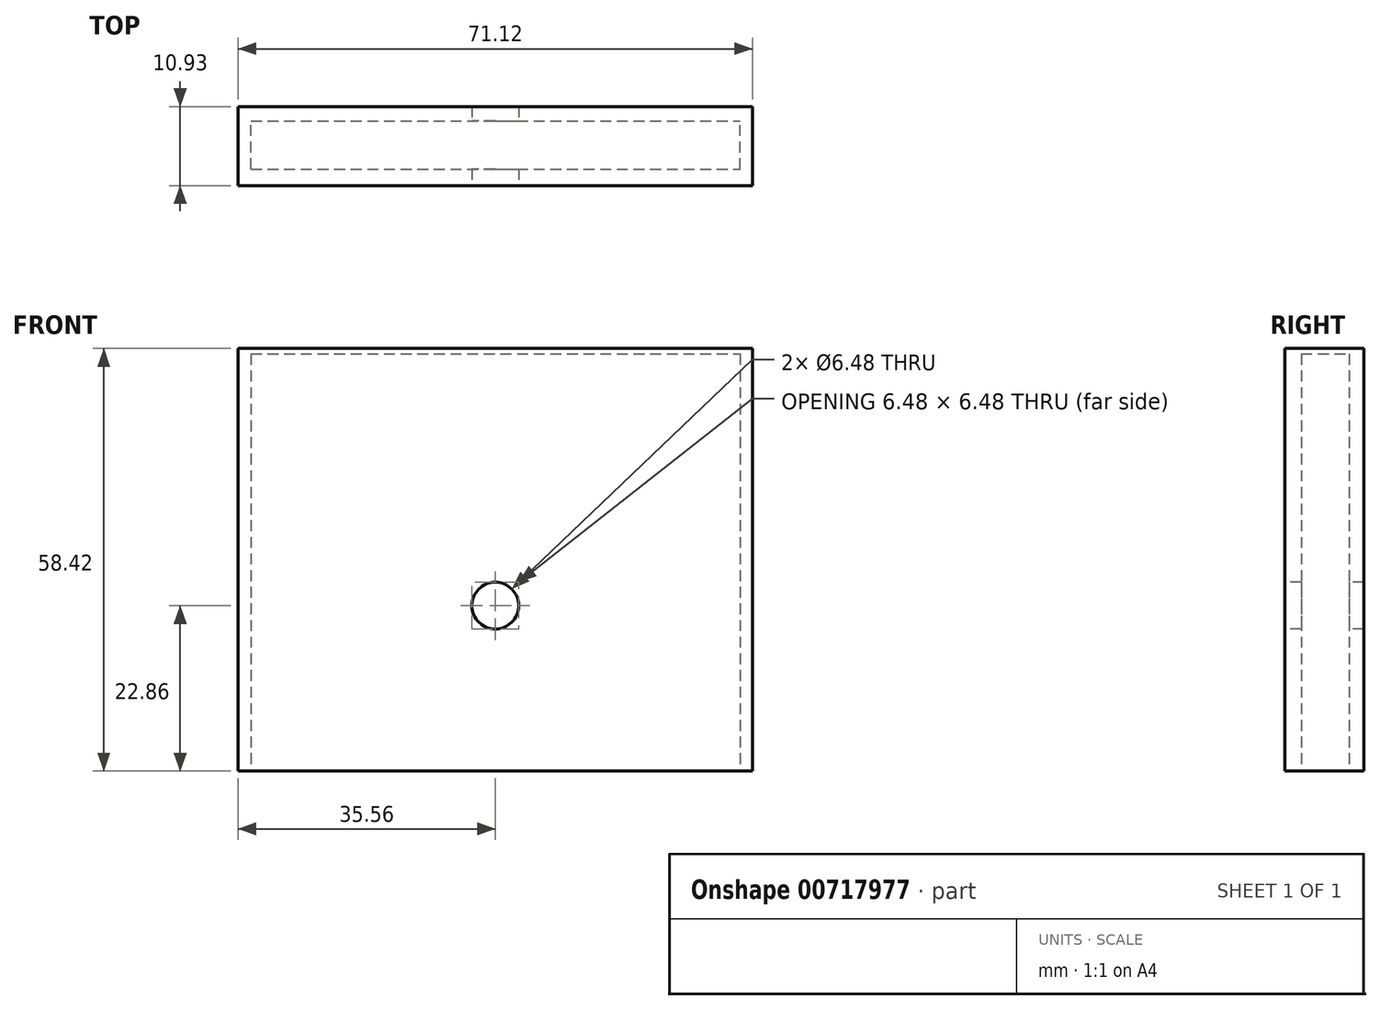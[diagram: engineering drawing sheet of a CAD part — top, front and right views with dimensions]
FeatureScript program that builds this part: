
annotation { "Feature Type Name" : "Feature", "Feature Type Description" : "" }
export const myFeature = defineFeature(function(context is Context, id is Id, definition is map)
    precondition{}
    {
        {
            var Q0;
            Q0=qCreatedBy(makeId("Front.planeOp"),FACE);
            var sketch = newSketch(context, id + "F0", { "sketchPlane" : qUnion([Q0])});
            skLineSegment(sketch, "E0", {"start": v(0, 0) * mm, "end": v(0, 35.56) * mm});
            skLineSegment(sketch, "E1", {"start": v(0, 35.56) * mm, "end": v(35.56, 35.56) * mm});
            skLineSegment(sketch, "E2", {"start": v(35.56, 35.56) * mm, "end": v(35.56, -22.86) * mm});
            skLineSegment(sketch, "E3", {"start": v(35.56, -22.86) * mm, "end": v(-35.56, -22.86) * mm});
            skLineSegment(sketch, "E4", {"start": v(-35.56, -22.86) * mm, "end": v(-35.56, 35.56) * mm});
            skLineSegment(sketch, "E5", {"start": v(-35.56, 35.56) * mm, "end": v(0, 35.56) * mm});
            skSolve(sketch);
        }
        {
            var Q0;
            Q0 = qSketchRegion(id + "F0", true);
            extrude(context, id + "F1", {"entities" : qUnion([Q0]), "depth" : 2.3 * mm, "offsetDistance" : 25.4 * mm});
        }
        {
            var Q0;
            Q0 = qSketchRegion(id + "F0", true);
            extrude(context, id + "F2", {"entities" : qUnion([Q0]), "operationType" : NewBodyOperationType.ADD, "oppositeDirection" : true, "depth" : 8.64 * mm, "offsetDistance" : 25.4 * mm});
        }
        {
            var Q0;
            {var subQ0=sQuery(id+"F0.wireOp",EDGE,"E3");Q0=makeQuery(id+"F2.boolean.opBoolean","MERGE",FACE,{"derivedFrom":[makeQuery(id+"F1.opExtrude","SWEPT_FACE",FACE,{"disambiguationData":[OSD([subQ0])]}),makeQuery(id+"F2.opExtrude","SWEPT_FACE",FACE,{"disambiguationData":[OSD([subQ0])]})]});}
            var sketch = newSketch(context, id + "F3", { "sketchPlane" : qUnion([Q0])});
            skLineSegment(sketch, "E6.bottom", {"start": v(-33.78, 0) * mm, "end": v(33.86, 0) * mm});
            skLineSegment(sketch, "E6.top", {"start": v(-33.78, -6.65) * mm, "end": v(33.86, -6.65) * mm});
            skLineSegment(sketch, "E6.left", {"start": v(-33.78, 0) * mm, "end": v(-33.78, -6.65) * mm});
            skLineSegment(sketch, "E6.right", {"start": v(33.86, 0) * mm, "end": v(33.86, -6.65) * mm});
            skSolve(sketch);
        }
        {
            var Q0;
            Q0 = qSketchRegion(id + "F3", true);
            extrude(context, id + "F4", {"entities" : qUnion([Q0]), "operationType" : NewBodyOperationType.REMOVE, "oppositeDirection" : true, "depth" : 57.66 * mm, "offsetDistance" : 25.4 * mm});
        }
        {
            var Q0;
            Q0=makeQuery(id+"F1.opExtrude","CAP_FACE",FACE,{"disambiguationData":[OSD([sQuery(id+"F0.wireOp",EDGE,"E1"),sQuery(id+"F0.wireOp",EDGE,"E2"),sQuery(id+"F0.wireOp",EDGE,"E3"),sQuery(id+"F0.wireOp",EDGE,"E4"),sQuery(id+"F0.wireOp",EDGE,"E5")])],"isStart":false});
            var sketch = newSketch(context, id + "F5", { "sketchPlane" : qUnion([Q0])});
            skCircle(sketch, "E7", {"center": v(0, 0) * mm, "radius": 3.24 * mm});
            skSolve(sketch);
        }
        {
            var Q0;
            Q0 = qSketchRegion(id + "F5", true);
            extrude(context, id + "F6", {"entities" : qUnion([Q0]), "operationType" : NewBodyOperationType.REMOVE, "oppositeDirection" : true, "depth" : 25.4 * mm, "offsetDistance" : 25.4 * mm});
        }
    });
